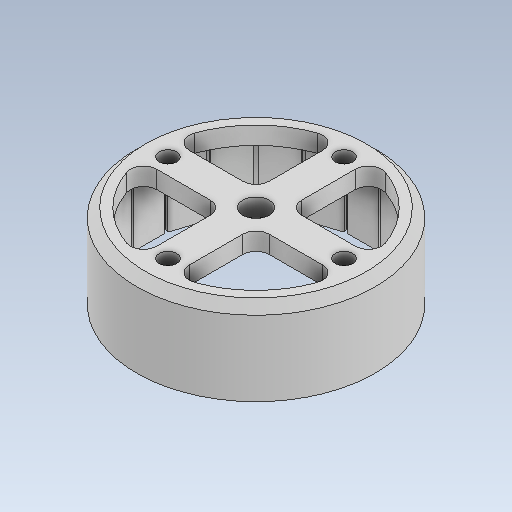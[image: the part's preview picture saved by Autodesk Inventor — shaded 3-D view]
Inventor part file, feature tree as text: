
AUTODESK INVENTOR PART (.ipt)
format: ipt  version: 2023 (Build 270158000, 158)  size: 289,280 bytes
history: native  units: mm
features: sketch x6, other x3
ambient origin geometry x8: Origin, YZ Plane, XZ Plane, XY Plane, X Axis, Y Axis, Z Axis, Center Point
bodies: Solid1 (feature_tree)
feature tree (9):
  other  "mot_27_1.ipt"
  other  "Solid1::mot_27_1.ipt"
  other  "TaggingFeature1"
  sketch  "Sketch1"  dims[d0=10.0mm]
  sketch  "Sketch2"
  sketch  "Sketch3"
  sketch  "Sketch4"
  sketch  "Sketch5"
  sketch  "Sketch6"
